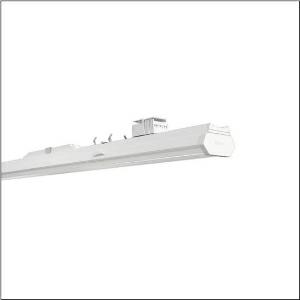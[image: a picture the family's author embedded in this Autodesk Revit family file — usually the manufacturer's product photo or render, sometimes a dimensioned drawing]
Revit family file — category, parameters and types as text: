
# Revit family: licross_r__21_protected_ho_52td12dn4e5md_1fe0
name_source: partatom
category: Lighting Fixtures
units: mm (PartAtom-declared; Revit-internal decimal feet)

## family parameters
Cut with Voids When Loaded = No
Host = Face
Light Source = No
Part Type = Normal
Room Calculation Point = No
Round Connector Dimension = Use Diameter
Shared = No

## types (1)
- --- (1 x LED, 2200 lm, 14.2 W, 4000K)
    Apparent Load = 14 VA
    CIE Flux Codes = 70 91 97 98 100
    Color Rendering = 80
    Color Temperature = 4000K
    Default Elevation = 1800 mm
    Description = Licross® 21 Protected HO, luminaire insert, of sheet steel, galvanised, coil coated, white, length: 1.500mm, width: 90mm, height: 103mm, LED rated luminous flux: 14.690lm, light colour: 840, control gear: DALI 2 (for two DALI lines), with plug, 6-pole, with phase selection, mains connection: 220..240V, AC/DC, 0/50..60Hz, rated input power: 85W, without changeover relay, for emergency light function, for central battery installations according to DIN EN 60598-2-22, internal wiring halogen-free, primary light control with lens, of plastic, primary optical cover: cover, of PMMA, light emission: direct distribution, primary light characteristic: symmetric, protection rating (complete): IP54, insulation class (complete): insulation class I (protective earthing), certification: CE, ENEC, VDE, UKCA, protection symbol: D if used in an environment with non-conductive dust loads with corresponding accessories, impact resistance: IK06, permissible ambient temperature for indoor applications: -25..+35°C, standard: EN 60598-2-22, corresponds to IFS (International Featured Standards) requirements for safety and quality in the food industry, reducing of maximum allowable ambient temperature of 5°C with ceiling mounting, LABS conformity tested according to VDMA 24364:2018-05, packaging unit: 1 piece
    Height = 92 mm
    Lamp = 1 x LED
    Lamp Light Flux = 2200 lm
    Lamp Power = 14.2 W
    Lamp count = 1
    Length = 1500 mm
    Luminous efficacy = 155 lm/W
    Manufacturer = Siteco
    ModVariant = No
    Model = 52TD12DN4E5MD
    Mounting Place = Ceiling
    Mounting Type = Pendant
    Number of Poles = 1
    OnlyDefault = Yes
    Power Factor = 1
    Product Name = Licross® 21 Protected HO
    Product group = luminaire insert | ceiling pendant
    ProductGroupID = 902
    Protection Class = Protection class I
    Protection Degree = IP 54
    RLX_Detail_Level = 1
    RLX_Emergency_Light_Flux = 0 lm
    RLX_Emergency_Type = 0
    RLX_Emergency_Type_DB = No
    RlxData = <blob elided: 25029 chars, md5=fa121ec1>
    Socket = socket
    Standby Power = 0 W
    System Light Flux = 2200 lm
    System Power = 14 W
    Type Comments = : DC mode (central or group accumulator) initial emergency light level
    Type Image = l_1256148.jpg
    URL = http://relux.com
    VarID = @adj_137869
    Voltage = 0 V
    Weight = 0.00 kg
    Width = 88 mm

## geometry (parser evidence)
native form markers: Blend x4, Sweep x9
no freeform markers — native parametric forms only
